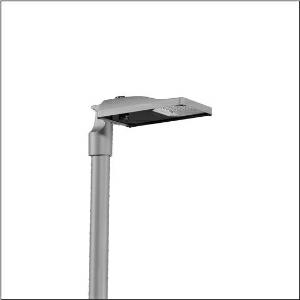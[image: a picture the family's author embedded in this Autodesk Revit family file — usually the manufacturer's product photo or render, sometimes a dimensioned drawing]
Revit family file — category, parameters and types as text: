
# Revit family: streetlight_sl_31_micro___st1_0a_5xh1d71t08ca_5556
name_source: partatom
category: Lighting Fixtures
units: mm (PartAtom-declared; Revit-internal decimal feet)

## family parameters
Cut with Voids When Loaded = No
Host = Face
Light Source = No
Part Type = Normal
Room Calculation Point = No
Round Connector Dimension = Use Diameter
Shared = No

## types (1)
- --- (1 x LED, 1170 lm, 10.2 W, 2200K)
    Apparent Load = 10 VA
    CIE Flux Codes = 37 72 97 100 100
    Color Rendering = 70
    Color Temperature = 2200K
    Default Elevation = 1800 mm
    Description = Streetlight SL 31 micro D4i, Desk-Remote mast luminaire for post-top, side-entry; light control with lens of PMMA; light distribution: ST1.0a, direct asymmetric distribution, for standard-compliant lighting for roads and squares; LED: luminous flux: 1.170lm, light colour: 722, colour temperature: 2200K; luminous efficacy: 114,7lm/W; control: pre-setting: logarithmic dimming characteristic, flexible luminous flux parameterisation, time-dependent luminous flux control, constant luminous flux control, power reduction, intelligent temperature release in ECG and LED module, overheat protection; luminaire housing, of diecast aluminium, Siteco® metallic grey (DB 702S), corrosivity category C5 high according to DIN EN ISO 12944; cover of toughened safety glass, transparent, mast flange of diecast aluminium, Siteco® metallic grey (DB 702S), spigot size: 76/60mm, mast flange included unmounted; with cable H07RN-F 2x 1.5mm², cable length: 5,5m, connection cable pre-assembled; mains connection: 220..240V, AC, 50/60Hz; power consumption (at start of service life): 10,2W / (at end of service life): 10,5W / (with reduced operation 50%): 5,3W; protection rating (complete): IP66; insulation class (complete): insulation class II (safety insulation); impact resistance: IK09; certification: CE, ENEC, ENEC+, VDE, UKCA, ZD4i; permissible operating ambient temperature for outdoor applications: -40..+50°C; packaging unit: 1 piece

Light Distribution: ST1.0a
    Height = 76 mm
    Lamp = 1 x LED
    Lamp Light Flux = 1170 lm
    Lamp Power = 10.2 W
    Lamp count = 1
    Length = 467 mm
    Luminous efficacy = 115 lm/W
    Manufacturer = Siteco
    ModVariant = No
    Model = 5XH1D71T08CA
    Number of Poles = 1
    OnlyDefault = Yes
    Power Factor = 1
    Product Name = Streetlight SL 31 micro | ST1.0a
    Product group = mast luminaire | pylon top
    ProductGroupID = 6100
    Protection Class = Protection class II
    Protection Degree = IP 66
    RLX_Detail_Level = 1
    RLX_Emergency_Light_Flux = 0 lm
    RLX_Emergency_Type = 0
    RLX_Emergency_Type_DB = No
    RlxData = <blob elided: 23317 chars, md5=c3e9842a>
    Socket = socket
    Standby Power = 0 W
    System Light Flux = 1170 lm
    System Power = 10 W
    Type Comments = factory setting: luminous flux: 100 % | dim-lin: 254 | 386 mA
    Type Image = l_1300315.jpg
    URL = http://relux.com
    VarID = @adj_008899
    Voltage = 0 V
    Weight = 0.00 kg
    Width = 265 mm

## geometry (parser evidence)
native form markers: Blend x4, Sweep x9
no freeform markers — native parametric forms only
